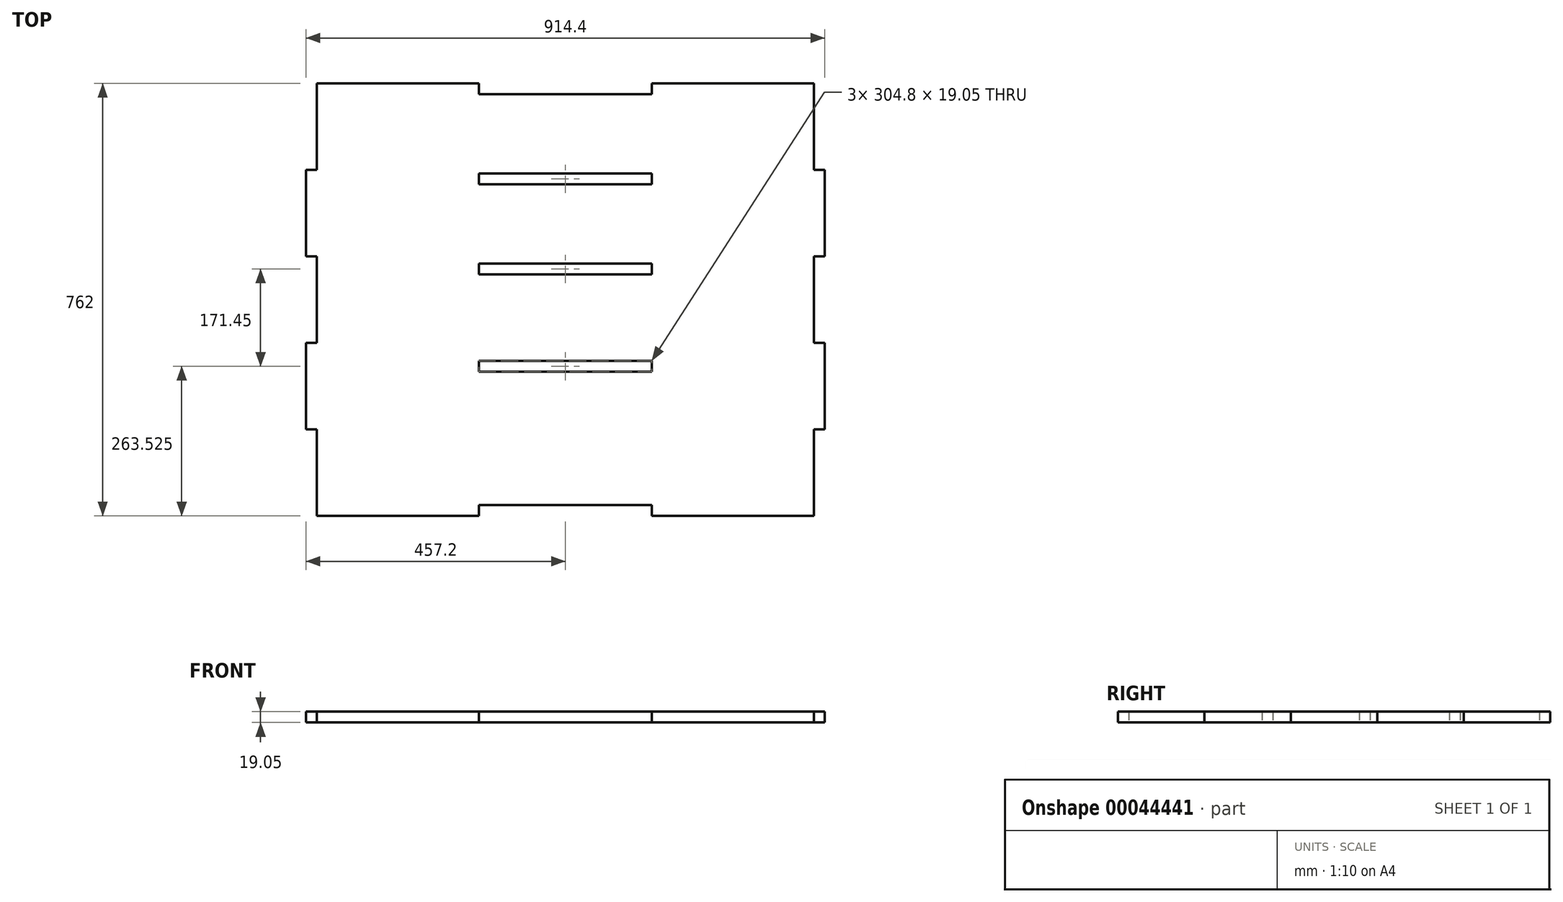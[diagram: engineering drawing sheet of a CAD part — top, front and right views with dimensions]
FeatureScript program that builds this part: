
annotation { "Feature Type Name" : "Feature", "Feature Type Description" : "" }
export const myFeature = defineFeature(function(context is Context, id is Id, definition is map)
    precondition{}
    {
        {
            var Q0;
            Q0=qCreatedBy(makeId("Top.planeOp"),FACE);
            var sketch = newSketch(context, id + "F0", { "sketchPlane" : qUnion([Q0])});
            skLineSegment(sketch, "E0.rect.bottom", {"start": v(-438.15, -381) * mm, "end": v(438.15, -381) * mm});
            skLineSegment(sketch, "E0.rect.top", {"start": v(-438.15, 381) * mm, "end": v(438.15, 381) * mm});
            skLineSegment(sketch, "E0.rect.left", {"start": v(-438.15, -381) * mm, "end": v(-438.15, 381) * mm});
            skLineSegment(sketch, "E0.rect.right", {"start": v(438.15, -381) * mm, "end": v(438.15, 381) * mm});
            skPoint(sketch, "E0.rect.middle", {"position": v(0, 0) * mm});
            skLineSegment(sketch, "E1.bottom", {"start": v(152.4, -107.95) * mm, "end": v(-152.4, -107.95) * mm});
            skLineSegment(sketch, "E1.top", {"start": v(152.4, -127) * mm, "end": v(-152.4, -127) * mm});
            skLineSegment(sketch, "E1.left", {"start": v(152.4, -107.95) * mm, "end": v(152.4, -127) * mm});
            skLineSegment(sketch, "E1.right", {"start": v(-152.4, -107.95) * mm, "end": v(-152.4, -127) * mm});
            skLineSegment(sketch, "E2.bottom", {"start": v(152.4, 63.5) * mm, "end": v(-152.4, 63.5) * mm});
            skLineSegment(sketch, "E2.top", {"start": v(152.4, 44.45) * mm, "end": v(-152.4, 44.45) * mm});
            skLineSegment(sketch, "E2.left", {"start": v(152.4, 63.5) * mm, "end": v(152.4, 44.45) * mm});
            skLineSegment(sketch, "E2.right", {"start": v(-152.4, 63.5) * mm, "end": v(-152.4, 44.45) * mm});
            skLineSegment(sketch, "E3.bottom", {"start": v(152.4, 222.25) * mm, "end": v(-152.4, 222.25) * mm});
            skLineSegment(sketch, "E3.top", {"start": v(152.4, 203.2) * mm, "end": v(-152.4, 203.2) * mm});
            skLineSegment(sketch, "E3.left", {"start": v(152.4, 222.25) * mm, "end": v(152.4, 203.2) * mm});
            skLineSegment(sketch, "E3.right", {"start": v(-152.4, 222.25) * mm, "end": v(-152.4, 203.2) * mm});
            skLineSegment(sketch, "E4.bottom", {"start": v(-438.15, 228.6) * mm, "end": v(-457.2, 228.6) * mm});
            skLineSegment(sketch, "E4.top", {"start": v(-438.15, 76.2) * mm, "end": v(-457.2, 76.2) * mm});
            skLineSegment(sketch, "E4.left", {"start": v(-438.15, 228.6) * mm, "end": v(-438.15, 76.2) * mm});
            skLineSegment(sketch, "E4.right", {"start": v(-457.2, 228.6) * mm, "end": v(-457.2, 76.2) * mm});
            skLineSegment(sketch, "E5.bottom", {"start": v(-457.2, -228.6) * mm, "end": v(-438.15, -228.6) * mm});
            skLineSegment(sketch, "E5.top", {"start": v(-457.2, -76.2) * mm, "end": v(-438.15, -76.2) * mm});
            skLineSegment(sketch, "E5.left", {"start": v(-457.2, -228.6) * mm, "end": v(-457.2, -76.2) * mm});
            skLineSegment(sketch, "E5.right", {"start": v(-438.15, -228.6) * mm, "end": v(-438.15, -76.2) * mm});
            skLineSegment(sketch, "E6.bottom", {"start": v(-152.4, -381) * mm, "end": v(152.4, -381) * mm});
            skLineSegment(sketch, "E6.top", {"start": v(-152.4, -361.95) * mm, "end": v(152.4, -361.95) * mm});
            skLineSegment(sketch, "E6.left", {"start": v(-152.4, -381) * mm, "end": v(-152.4, -361.95) * mm});
            skLineSegment(sketch, "E6.right", {"start": v(152.4, -381) * mm, "end": v(152.4, -361.95) * mm});
            skLineSegment(sketch, "E7.bottom", {"start": v(-152.4, 381) * mm, "end": v(152.4, 381) * mm});
            skLineSegment(sketch, "E7.top", {"start": v(-152.4, 361.95) * mm, "end": v(152.4, 361.95) * mm});
            skLineSegment(sketch, "E7.left", {"start": v(-152.4, 381) * mm, "end": v(-152.4, 361.95) * mm});
            skLineSegment(sketch, "E7.right", {"start": v(152.4, 381) * mm, "end": v(152.4, 361.95) * mm});
            skLineSegment(sketch, "E8.MirrorCS", {"start": v(438.15, 228.6) * mm, "end": v(457.2, 228.6) * mm});
            skLineSegment(sketch, "E9.MirrorCS", {"start": v(457.2, -228.6) * mm, "end": v(438.15, -228.6) * mm});
            skLineSegment(sketch, "E10.MirrorCS", {"start": v(438.15, 76.2) * mm, "end": v(457.2, 76.2) * mm});
            skLineSegment(sketch, "E11.MirrorCS", {"start": v(457.2, -76.2) * mm, "end": v(438.15, -76.2) * mm});
            skLineSegment(sketch, "E12.MirrorCS", {"start": v(438.15, 228.6) * mm, "end": v(438.15, 76.2) * mm});
            skLineSegment(sketch, "E13.MirrorCS", {"start": v(457.2, -228.6) * mm, "end": v(457.2, -76.2) * mm});
            skLineSegment(sketch, "E14.MirrorCS", {"start": v(438.15, -228.6) * mm, "end": v(438.15, -76.2) * mm});
            skLineSegment(sketch, "E15.MirrorCS", {"start": v(457.2, 228.6) * mm, "end": v(457.2, 76.2) * mm});
            skSolve(sketch);
        }
        {
            var Q0;
            {var subQ0=sQuery(id+"F0.wireOp",EDGE,"E0.rect.bottom");Q0=makeQuery(id+"F0.imprint","IMPRINT",FACE,{"disambiguationData":[TD([[makeQuery(id+"F0.imprint","IMPRINT",EDGE,{"derivedFrom":subQ0}),1.0]])]});}
            var Q1;
            Q1=makeQuery(id+"F0.imprint","IMPRINT",FACE,{"disambiguationData":[TD([[makeQuery(id+"F0.imprint","IMPRINT",EDGE,{"derivedFrom":sQuery(id+"F0.wireOp",EDGE,"E4.bottom")}),1.0]])]});
            var Q2;
            Q2=makeQuery(id+"F0.imprint","IMPRINT",FACE,{"disambiguationData":[TD([[makeQuery(id+"F0.imprint","IMPRINT",EDGE,{"derivedFrom":sQuery(id+"F0.wireOp",EDGE,"E5.bottom")}),1.0]])]});
            var Q3;
            Q3=makeQuery(id+"F0.imprint","IMPRINT",FACE,{"disambiguationData":[TD([[makeQuery(id+"F0.imprint","IMPRINT",EDGE,{"derivedFrom":sQuery(id+"F0.wireOp",EDGE,"E8.MirrorCS")}),-1.0]])]});
            var Q4;
            Q4=makeQuery(id+"F0.imprint","IMPRINT",FACE,{"disambiguationData":[TD([[makeQuery(id+"F0.imprint","IMPRINT",EDGE,{"derivedFrom":sQuery(id+"F0.wireOp",EDGE,"E9.MirrorCS")}),-1.0]])]});
            extrude(context, id + "F1", {"entities" : qUnion([Q0, Q1, Q2, Q3, Q4]), "depth" : 19.05 * mm});
        }
    });
